# Revit family: Runtal-UFLT-5
name_source: partatom
category: Generic Models
units: mm (PartAtom-declared; Revit-internal decimal feet)

## family parameters
Can host rebar = No
Cut with Voids When Loaded = No
Host = Face
Maintain Annotation Orientation = No
Part Type = Normal
Room Calculation Point = No
Round Connector Dimension = Use Diameter
Shared = No

## types (1)
- Runtal-UFLT-5
    Assembly Code = D3020
    Default Elevation = 4' - 0"
    Description = UFLT panel radiators are manufactured in the USA from cold rolled steel. The panels are finished in gloss powdercoat and available in many standard colors and over 100 optional colors. These panels are made in lengths from 2’-0” to 24’-0”, and heights from 5 7/8” to 14 3/8”. Standard piping connections are 1/2” NPT for inlet and outlet piping, and 1/8” NPT for vents. For more complete UFLT specifications, please refer to the Runtal technical pages.
    Fins = Powder Coated-Runtal-W-White
    Length = 2' - 0"
    Manufacturer = Runtal Radiators
    Model = UFLT-5
    Radiator = Steel, Paint Finish, Ivory, Glossy
    URL = http://www.runtalnorthamerica.com

## geometry (parser evidence)
native form markers: Sweep x38
no freeform markers — native parametric forms only
